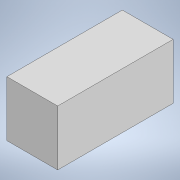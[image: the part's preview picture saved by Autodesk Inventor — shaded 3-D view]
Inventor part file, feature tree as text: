
AUTODESK INVENTOR PART (.ipt)
format: ipt  version: 2020 (Build 240168000, 168)  size: 84,480 bytes
history: native  units: in
note: dims shown in document units (in); Inventor stores cm internally (conversion verified against a paired STEP export)
features: extrude x1, sketch x1
ambient origin geometry x8: Origin, YZ Plane, XZ Plane, XY Plane, X Axis, Y Axis, Z Axis, Center Point
bodies: Solid1 (feature_tree)
feature tree (2):
  extrude  "Extrusion1"  Depth=0.9843in
  sketch  "Sketch1"  dims[d0=0.4331in d1=0.9843in d2=0.4724in d3=0.0in]
